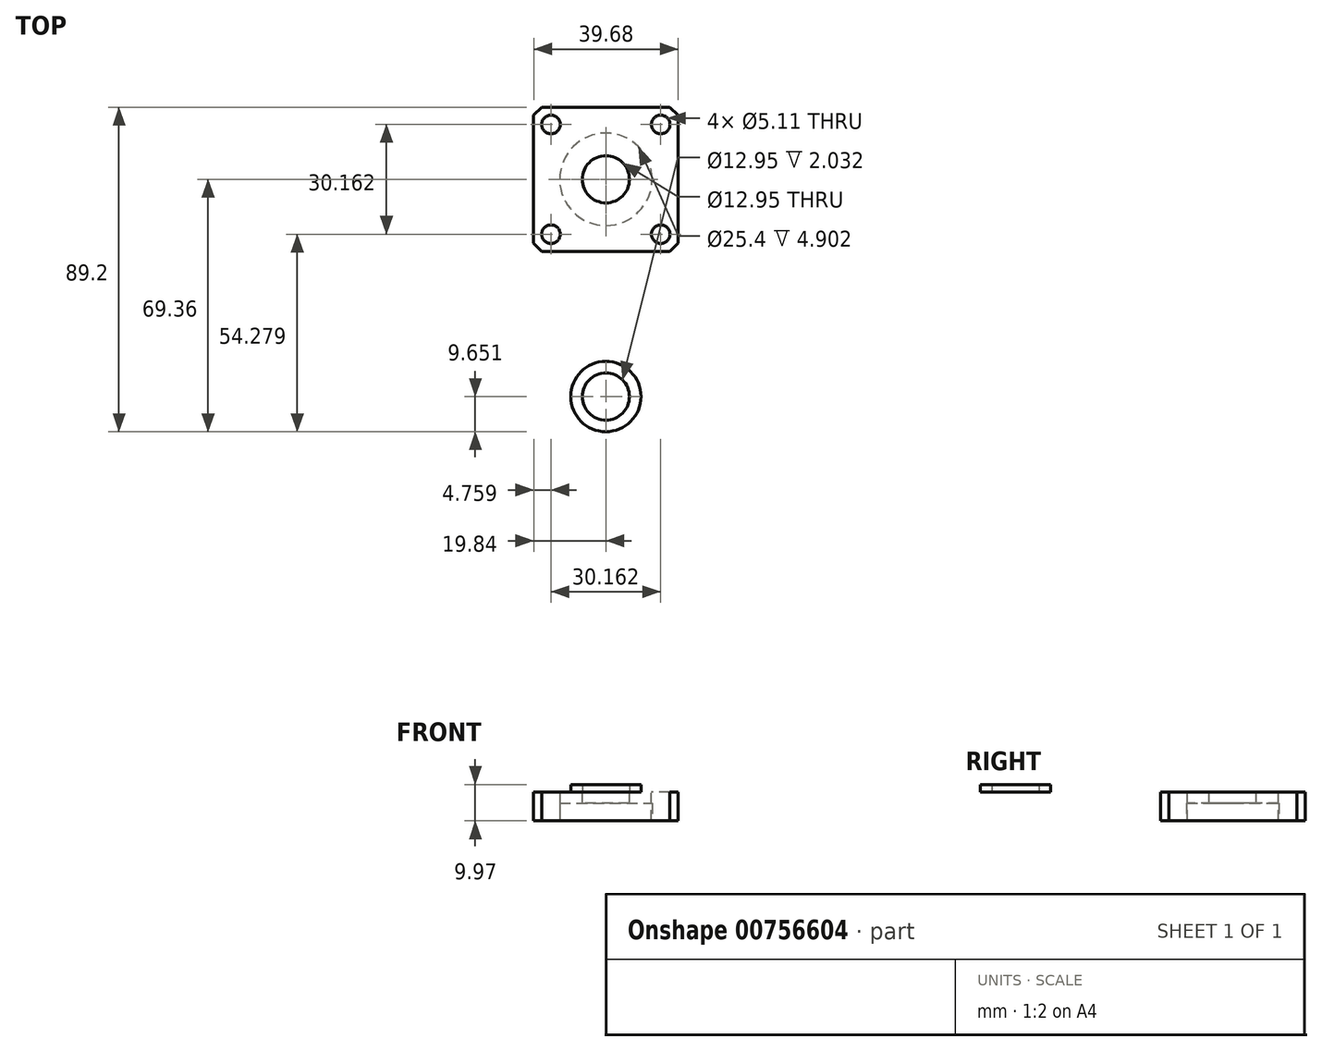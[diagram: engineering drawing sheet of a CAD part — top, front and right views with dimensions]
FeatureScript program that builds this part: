
annotation { "Feature Type Name" : "Feature", "Feature Type Description" : "" }
export const myFeature = defineFeature(function(context is Context, id is Id, definition is map)
    precondition{}
    {
        {
            var Q0;
            Q0=qCreatedBy(makeId("Top.planeOp"),FACE);
            var sketch = newSketch(context, id + "F0", { "sketchPlane" : qUnion([Q0])});
            skLineSegment(sketch, "E0.bottom", {"start": v(19.84, -19.84) * mm, "end": v(-19.84, -19.84) * mm});
            skLineSegment(sketch, "E0.top", {"start": v(19.84, 19.84) * mm, "end": v(-19.84, 19.84) * mm});
            skLineSegment(sketch, "E0.left", {"start": v(19.84, -19.84) * mm, "end": v(19.84, 19.84) * mm});
            skLineSegment(sketch, "E0.right", {"start": v(-19.84, -19.84) * mm, "end": v(-19.84, 19.84) * mm});
            skPoint(sketch, "E0.middle", {"position": v(0, 0) * mm});
            skCircle(sketch, "E1", {"center": v(0, 0) * mm, "radius": 12.7 * mm});
            skCircle(sketch, "E2", {"center": v(0, 0) * mm, "radius": 6.48 * mm});
            skPoint(sketch, "E3", {"position": v(-15.08, 15.08) * mm});
            skPoint(sketch, "E4.MirrorP", {"position": v(15.08, 15.08) * mm});
            skPoint(sketch, "E5.MirrorP", {"position": v(-15.08, -15.08) * mm});
            skPoint(sketch, "E6.MirrorP", {"position": v(15.08, -15.08) * mm});
            skCircle(sketch, "E7", {"center": v(0, -59.7) * mm, "radius": 9.65 * mm});
            skCircle(sketch, "E8", {"center": v(0, -59.7) * mm, "radius": 6.48 * mm});
            skSolve(sketch);
        }
        {
            var Q0;
            Q0=makeQuery(id+"F0.imprint","IMPRINT",FACE,{"disambiguationData":[TD([[makeQuery(id+"F0.imprint","IMPRINT",EDGE,{"derivedFrom":sQuery(id+"F0.wireOp",EDGE,"E0.bottom")}),-1.0]])]});
            var Q1;
            Q1=makeQuery(id+"F0.imprint","IMPRINT",FACE,{"disambiguationData":[TD([[makeQuery(id+"F0.imprint","IMPRINT",EDGE,{"derivedFrom":sQuery(id+"F0.wireOp",EDGE,"E1")}),1.0]])]});
            extrude(context, id + "F1", {"entities" : qUnion([Q0, Q1]), "oppositeDirection" : true, "depth" : 7.94 * mm, "offsetDistance" : 25.4 * mm});
        }
        {
            var Q0;
            Q0=makeQuery(id+"F1.opExtrude","CAP_FACE",FACE,{"disambiguationData":[OSD([sQuery(id+"F0.wireOp",EDGE,"E0.bottom"),sQuery(id+"F0.wireOp",EDGE,"E0.top"),sQuery(id+"F0.wireOp",EDGE,"E0.left"),sQuery(id+"F0.wireOp",EDGE,"E0.right"),sQuery(id+"F0.wireOp",EDGE,"E2")])],"isStart":false});
            var sketch = newSketch(context, id + "F2", { "sketchPlane" : qUnion([Q0])});
            skCircle(sketch, "E9", {"center": v(0, 0) * mm, "radius": 12.7 * mm});
            skSolve(sketch);
        }
        {
            var Q0;
            Q0=makeQuery(id+"F2.imprint","IMPRINT",FACE,{"disambiguationData":[TD([[makeQuery(id+"F2.imprint","IMPRINT",EDGE,{"derivedFrom":sQuery(id+"F2.wireOp",EDGE,"E9")}),1.0]])]});
            extrude(context, id + "F3", {"entities" : qUnion([Q0]), "operationType" : NewBodyOperationType.REMOVE, "oppositeDirection" : true, "depth" : 4.9 * mm, "offsetDistance" : 25.4 * mm});
        }
        {
            var Q0;
            Q0=sQuery(id+"F0.wireOp",VERTEX,"E5.MirrorP");
            var Q1;
            Q1=sQuery(id+"F0.wireOp",VERTEX,"E6.MirrorP");
            var Q2;
            Q2=sQuery(id+"F0.wireOp",VERTEX,"E4.MirrorP");
            var Q3;
            Q3=sQuery(id+"F0.wireOp",VERTEX,"E3");
            var Q4;
            Q4=makeQuery(id+"F1.opExtrude","SWEPT_BODY",BODY,{"disambiguationData":[OSD([sQuery(id+"F0.wireOp",EDGE,"E0.bottom"),sQuery(id+"F0.wireOp",EDGE,"E0.top"),sQuery(id+"F0.wireOp",EDGE,"E0.left"),sQuery(id+"F0.wireOp",EDGE,"E0.right"),sQuery(id+"F0.wireOp",EDGE,"E2")])]});
            hole(context, id + "F4", {"style" : HoleStyle.SIMPLE, "endStyle" : HoleEndStyle.THROUGH, "standardTappedOrClearance" : lookupTablePath({ "standard" : "ANSI", "fit" : "Normal (ASME)", "size" : "#10", "type" : "Clearance" }), "standardBlindInLast" : lookupTablePath({ "fit" : "Free", "standard" : "ANSI", "size" : "#10", "type" : "Clearance" }), "holeDiameter" : 5.1 * mm, "majorDiameter" : 6.35 * mm, "isTappedThrough" : true, "tappedDepth" : 12.7 * mm, "tapClearance" : 3, "locations" : qUnion([Q0, Q1, Q2, Q3]), "scope" : qUnion([Q4])});
        }
        {
            var Q0;
            Q0=makeQuery(id+"F1.opExtrude","SWEPT_EDGE",EDGE,{"disambiguationData":[OSD([sQuery(id+"F0.wireOp",EDGE,"E0.bottom"),sQuery(id+"F0.wireOp",EDGE,"E0.right")])]});
            var Q1;
            Q1=makeQuery(id+"F1.opExtrude","SWEPT_EDGE",EDGE,{"disambiguationData":[OSD([sQuery(id+"F0.wireOp",EDGE,"E0.top"),sQuery(id+"F0.wireOp",EDGE,"E0.right")])]});
            var Q2;
            Q2=makeQuery(id+"F1.opExtrude","SWEPT_EDGE",EDGE,{"disambiguationData":[OSD([sQuery(id+"F0.wireOp",EDGE,"E0.top"),sQuery(id+"F0.wireOp",EDGE,"E0.left")])]});
            var Q3;
            Q3=makeQuery(id+"F1.opExtrude","SWEPT_EDGE",EDGE,{"disambiguationData":[OSD([sQuery(id+"F0.wireOp",EDGE,"E0.bottom"),sQuery(id+"F0.wireOp",EDGE,"E0.left")])]});
            chamfer(context, id + "F5", {"entities" : qUnion([Q0, Q1, Q2, Q3]), "width" : 2.25 * mm, "tangentPropagation" : true});
        }
        {
            var Q0;
            Q0=makeQuery(id+"F0.imprint","IMPRINT",FACE,{"disambiguationData":[TD([[makeQuery(id+"F0.imprint","IMPRINT",EDGE,{"derivedFrom":sQuery(id+"F0.wireOp",EDGE,"E7")}),1.0]])]});
            extrude(context, id + "F6", {"entities" : qUnion([Q0]), "depth" : 2.03 * mm, "offsetDistance" : 25.4 * mm});
        }
    });
